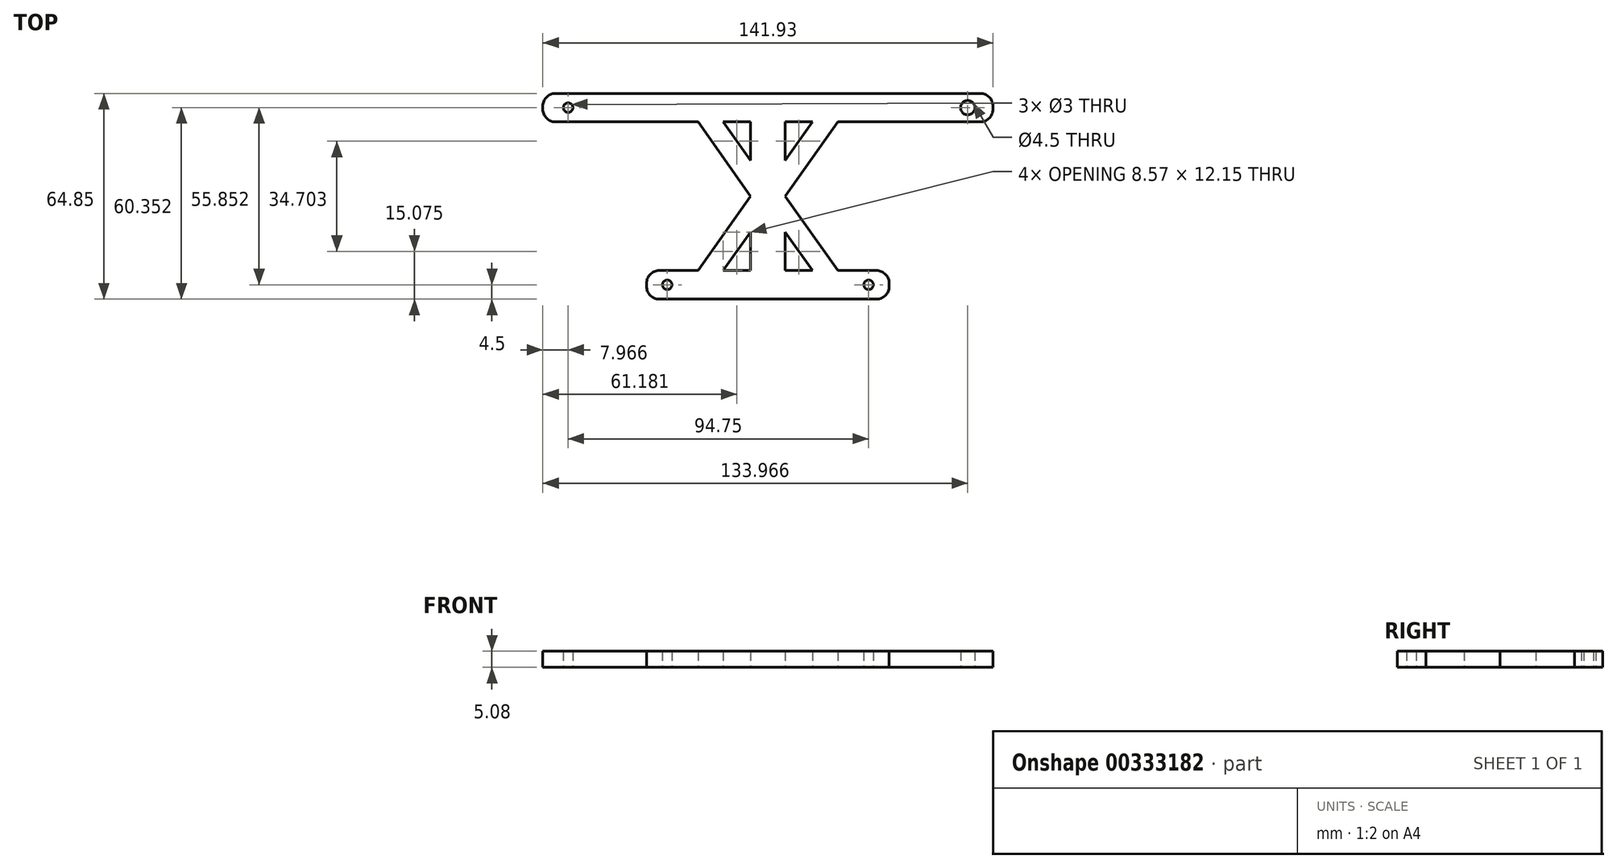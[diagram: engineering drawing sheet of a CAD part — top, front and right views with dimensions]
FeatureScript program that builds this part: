
annotation { "Feature Type Name" : "Feature", "Feature Type Description" : "" }
export const myFeature = defineFeature(function(context is Context, id is Id, definition is map)
    precondition{}
    {
        {
            var Q0;
            Q0=qCreatedBy(makeId("Top.planeOp"),FACE);
            var sketch = newSketch(context, id + "F0", { "sketchPlane" : qUnion([Q0])});
            skCircle(sketch, "E0", {"center": v(-52.08, 55.85) * mm, "radius": 1.5 * mm});
            skCircle(sketch, "E1", {"center": v(-20.83, 0) * mm, "radius": 1.5 * mm});
            skLineSegment(sketch, "E2", {"start": v(-20.83, 0) * mm, "end": v(10.92, 0) * mm});
            skLineSegment(sketch, "E3", {"start": v(-20.83, 0) * mm, "end": v(-52.08, 55.85) * mm});
            skLineSegment(sketch, "E4", {"start": v(-52.08, 55.85) * mm, "end": v(10.92, 55.85) * mm});
            skPoint(sketch, "E5.middle", {"position": v(10.92, 55.85) * mm});
            skPoint(sketch, "E6.middle", {"position": v(10.92, 0) * mm});
            skLineSegment(sketch, "E7", {"start": v(10.92, 0) * mm, "end": v(10.92, 55.85) * mm});
            skPoint(sketch, "E8.middle", {"position": v(10.92, 27.93) * mm});
            skLineSegment(sketch, "E9.MirrorCS", {"start": v(73.92, 55.85) * mm, "end": v(10.92, 55.85) * mm});
            skLineSegment(sketch, "E10.MirrorCS", {"start": v(42.67, 0) * mm, "end": v(73.92, 55.85) * mm});
            skLineSegment(sketch, "E11.MirrorCS", {"start": v(42.67, 0) * mm, "end": v(10.92, 0) * mm});
            skCircle(sketch, "E12.MirrorC", {"center": v(42.67, 0) * mm, "radius": 1.5 * mm});
            skPoint(sketch, "E13.middle", {"position": v(73.92, 55.85) * mm});
            skCircle(sketch, "E14", {"center": v(73.92, 55.85) * mm, "radius": 2.25 * mm});
            skLineSegment(sketch, "E15.bottom", {"start": v(81.88, 60.35) * mm, "end": v(-60.05, 60.35) * mm});
            skLineSegment(sketch, "E15.top", {"start": v(81.88, 51.35) * mm, "end": v(-60.05, 51.35) * mm});
            skLineSegment(sketch, "E15.left", {"start": v(81.88, 60.35) * mm, "end": v(81.88, 51.35) * mm});
            skLineSegment(sketch, "E15.right", {"start": v(-60.05, 60.35) * mm, "end": v(-60.05, 51.35) * mm});
            skLineSegment(sketch, "E16.bottom", {"start": v(49.17, 4.5) * mm, "end": v(-27.34, 4.5) * mm});
            skLineSegment(sketch, "E16.top", {"start": v(49.17, -4.5) * mm, "end": v(-27.34, -4.5) * mm});
            skLineSegment(sketch, "E16.left", {"start": v(49.17, 4.5) * mm, "end": v(49.17, -4.5) * mm});
            skLineSegment(sketch, "E16.right", {"start": v(-27.34, 4.5) * mm, "end": v(-27.34, -4.5) * mm});
            skLineSegment(sketch, "E17", {"start": v(5.42, 51.35) * mm, "end": v(5.42, 4.5) * mm});
            skLineSegment(sketch, "E18.MirrorCS", {"start": v(16.42, 51.35) * mm, "end": v(16.42, 4.5) * mm});
            skLineSegment(sketch, "E19", {"start": v(5.42, 27.93) * mm, "end": v(16.42, 27.93) * mm});
            skLineSegment(sketch, "E20", {"start": v(-11.1, 51.35) * mm, "end": v(5.42, 27.93) * mm});
            skLineSegment(sketch, "E21", {"start": v(-3.15, 51.35) * mm, "end": v(5.42, 39.2) * mm});
            skLineSegment(sketch, "E22.MirrorCS", {"start": v(24.99, 51.35) * mm, "end": v(16.42, 39.2) * mm});
            skLineSegment(sketch, "E23.MirrorCS", {"start": v(32.94, 51.35) * mm, "end": v(16.42, 27.93) * mm});
            skLineSegment(sketch, "E24.MirrorCS", {"start": v(32.94, 4.5) * mm, "end": v(16.42, 27.93) * mm});
            skLineSegment(sketch, "E25.MirrorCS", {"start": v(24.99, 4.5) * mm, "end": v(16.42, 16.65) * mm});
            skLineSegment(sketch, "E26.MirrorCS", {"start": v(-3.15, 4.5) * mm, "end": v(5.42, 16.65) * mm});
            skLineSegment(sketch, "E27.MirrorCS", {"start": v(-11.1, 4.5) * mm, "end": v(5.42, 27.93) * mm});
            skSolve(sketch);
        }
        {
            var Q0;
            {var subQ5=sQuery(id+"F0.wireOp",EDGE,"E0");var subQ7=sQuery(id+"F0.wireOp",EDGE,"E3");var subQ8=makeQuery(id+"F0.imprint","INTERSECT",VERTEX,{"derivedFrom":[subQ5,subQ7]});Q0=makeQuery(id+"F0.imprint","IMPRINT",FACE,{"disambiguationData":[TD([[makeQuery(id+"F0.imprint","IMPRINT",EDGE,{"disambiguationData":[TD([[subQ8,-1.0]])],"derivedFrom":subQ5}),-1.0]])]});}
            var Q1;
            {var subQ1=sQuery(id+"F0.wireOp",EDGE,"E2");var subQ5=sQuery(id+"F0.wireOp",EDGE,"E1");var subQ6=makeQuery(id+"F0.imprint","INTERSECT",VERTEX,{"derivedFrom":[subQ5,subQ1]});Q1=makeQuery(id+"F0.imprint","IMPRINT",FACE,{"disambiguationData":[TD([[makeQuery(id+"F0.imprint","IMPRINT",EDGE,{"disambiguationData":[TD([[subQ6,-1.0]])],"derivedFrom":subQ5}),-1.0]])]});}
            var Q2;
            Q2=makeQuery(id+"F0.imprint","IMPRINT",FACE,{"disambiguationData":[TD([[makeQuery(id+"F0.imprint","IMPRINT",EDGE,{"derivedFrom":sQuery(id+"F0.wireOp",EDGE,"E15.bottom")}),1.0]])]});
            var Q3;
            Q3=makeQuery(id+"F0.imprint","IMPRINT",FACE,{"disambiguationData":[TD([[makeQuery(id+"F0.imprint","IMPRINT",EDGE,{"derivedFrom":sQuery(id+"F0.wireOp",EDGE,"E16.top")}),-1.0]])]});
            var Q4;
            {var subQ1=sQuery(id+"F0.wireOp",EDGE,"E10.MirrorCS");var subQ5=sQuery(id+"F0.wireOp",EDGE,"E16.bottom");var subQ6=makeQuery(id+"F0.imprint","INTERSECT",VERTEX,{"derivedFrom":[subQ1,subQ5]});Q4=makeQuery(id+"F0.imprint","IMPRINT",FACE,{"disambiguationData":[TD([[makeQuery(id+"F0.imprint","IMPRINT",EDGE,{"disambiguationData":[TD([[subQ6,1.0]])],"derivedFrom":subQ1}),1.0]])]});}
            var Q5;
            {var subQ0=sQuery(id+"F0.wireOp",EDGE,"E15.top");var subQ1=sQuery(id+"F0.wireOp",EDGE,"E10.MirrorCS");var subQ2=makeQuery(id+"F0.imprint","INTERSECT",VERTEX,{"derivedFrom":[subQ1,subQ0]});Q5=makeQuery(id+"F0.imprint","IMPRINT",FACE,{"disambiguationData":[TD([[makeQuery(id+"F0.imprint","IMPRINT",EDGE,{"disambiguationData":[TD([[subQ2,-1.0]])],"derivedFrom":subQ1}),1.0]])]});}
            var Q6;
            {var subQ5=sQuery(id+"F0.wireOp",EDGE,"E17");Q6=makeQuery(id+"F0.imprint","IMPRINT",FACE,{"disambiguationData":[TD([[makeQuery(id+"F0.imprint","IMPRINT",EDGE,{"derivedFrom":subQ5}),1.0]])]});}
            var Q7;
            {var subQ5=sQuery(id+"F0.wireOp",EDGE,"E18.MirrorCS");Q7=makeQuery(id+"F0.imprint","IMPRINT",FACE,{"disambiguationData":[TD([[makeQuery(id+"F0.imprint","IMPRINT",EDGE,{"derivedFrom":subQ5}),-1.0]])]});}
            var Q8;
            {var subQ0=sQuery(id+"F0.wireOp",EDGE,"feb966cf-f615-44a7-a13d-1bd144c4b3750.MirrorCS");Q8=makeQuery(id+"F0.imprint","IMPRINT",FACE,{"disambiguationData":[TD([[makeQuery(id+"F0.imprint","IMPRINT",EDGE,{"derivedFrom":subQ0}),-1.0]])]});}
            var Q9;
            {var subQ0=sQuery(id+"F0.wireOp",EDGE,"d3fe900e-5d7e-4329-a638-1e34b492a3660.MirrorCS");Q9=makeQuery(id+"F0.imprint","IMPRINT",FACE,{"disambiguationData":[TD([[makeQuery(id+"F0.imprint","IMPRINT",EDGE,{"derivedFrom":subQ0}),1.0]])]});}
            var Q10;
            {var subQ0=sQuery(id+"F0.wireOp",EDGE,"hfX9tZ72-0kb9-5i1I-bADh-dzFUvOyJdu75");Q10=makeQuery(id+"F0.imprint","IMPRINT",FACE,{"disambiguationData":[TD([[makeQuery(id+"F0.imprint","IMPRINT",EDGE,{"derivedFrom":subQ0}),-1.0]])]});}
            var Q11;
            {var subQ0=sQuery(id+"F0.wireOp",EDGE,"7ac03fb2-961d-4cd1-b936-0828aa2fb5720.MirrorCS");Q11=makeQuery(id+"F0.imprint","IMPRINT",FACE,{"disambiguationData":[TD([[makeQuery(id+"F0.imprint","IMPRINT",EDGE,{"derivedFrom":subQ0}),-1.0]])]});}
            var Q12;
            {var subQ0=sQuery(id+"F0.wireOp",EDGE,"E20");Q12=makeQuery(id+"F0.imprint","IMPRINT",FACE,{"disambiguationData":[TD([[makeQuery(id+"F0.imprint","IMPRINT",EDGE,{"derivedFrom":subQ0}),1.0]])]});}
            var Q13;
            {var subQ0=sQuery(id+"F0.wireOp",EDGE,"E26.MirrorCS");Q13=makeQuery(id+"F0.imprint","IMPRINT",FACE,{"disambiguationData":[TD([[makeQuery(id+"F0.imprint","IMPRINT",EDGE,{"derivedFrom":subQ0}),1.0]])]});}
            var Q14;
            {var subQ0=sQuery(id+"F0.wireOp",EDGE,"E24.MirrorCS");Q14=makeQuery(id+"F0.imprint","IMPRINT",FACE,{"disambiguationData":[TD([[makeQuery(id+"F0.imprint","IMPRINT",EDGE,{"derivedFrom":subQ0}),1.0]])]});}
            var Q15;
            {var subQ0=sQuery(id+"F0.wireOp",EDGE,"E22.MirrorCS");Q15=makeQuery(id+"F0.imprint","IMPRINT",FACE,{"disambiguationData":[TD([[makeQuery(id+"F0.imprint","IMPRINT",EDGE,{"derivedFrom":subQ0}),1.0]])]});}
            extrude(context, id + "F1", {"entities" : qUnion([Q0, Q1, Q2, Q3, Q4, Q5, Q6, Q7, Q8, Q9, Q10, Q11, Q12, Q13, Q14, Q15]), "depth" : 5.08 * mm});
        }
        {
            var Q0;
            Q0=makeQuery(id+"F1.opExtrude","SWEPT_EDGE",EDGE,{"disambiguationData":[OSD([sQuery(id+"F0.wireOp",EDGE,"E15.bottom"),sQuery(id+"F0.wireOp",EDGE,"E15.right")])]});
            var Q1;
            Q1=makeQuery(id+"F1.opExtrude","SWEPT_EDGE",EDGE,{"disambiguationData":[OSD([sQuery(id+"F0.wireOp",EDGE,"E15.top"),sQuery(id+"F0.wireOp",EDGE,"E15.right")])]});
            var Q2;
            Q2=makeQuery(id+"F1.opExtrude","SWEPT_EDGE",EDGE,{"disambiguationData":[OSD([sQuery(id+"F0.wireOp",EDGE,"E15.bottom"),sQuery(id+"F0.wireOp",EDGE,"E15.left")])]});
            var Q3;
            Q3=makeQuery(id+"F1.opExtrude","SWEPT_EDGE",EDGE,{"disambiguationData":[OSD([sQuery(id+"F0.wireOp",EDGE,"E15.top"),sQuery(id+"F0.wireOp",EDGE,"E15.left")])]});
            var Q4;
            Q4=makeQuery(id+"F1.opExtrude","SWEPT_EDGE",EDGE,{"disambiguationData":[OSD([sQuery(id+"F0.wireOp",EDGE,"E16.bottom"),sQuery(id+"F0.wireOp",EDGE,"E16.left")])]});
            var Q5;
            Q5=makeQuery(id+"F1.opExtrude","SWEPT_EDGE",EDGE,{"disambiguationData":[OSD([sQuery(id+"F0.wireOp",EDGE,"E16.top"),sQuery(id+"F0.wireOp",EDGE,"E16.left")])]});
            var Q6;
            Q6=makeQuery(id+"F1.opExtrude","SWEPT_EDGE",EDGE,{"disambiguationData":[OSD([sQuery(id+"F0.wireOp",EDGE,"E16.bottom"),sQuery(id+"F0.wireOp",EDGE,"E16.right")])]});
            var Q7;
            Q7=makeQuery(id+"F1.opExtrude","SWEPT_EDGE",EDGE,{"disambiguationData":[OSD([sQuery(id+"F0.wireOp",EDGE,"E16.top"),sQuery(id+"F0.wireOp",EDGE,"E16.right")])]});
            fillet(context, id + "F2", {"entities" : qUnion([Q0, Q1, Q2, Q3, Q4, Q5, Q6, Q7]), "radius" : 4 * mm, "tangentPropagation" : true, "allowEdgeOverflow" : false});
        }
    });
